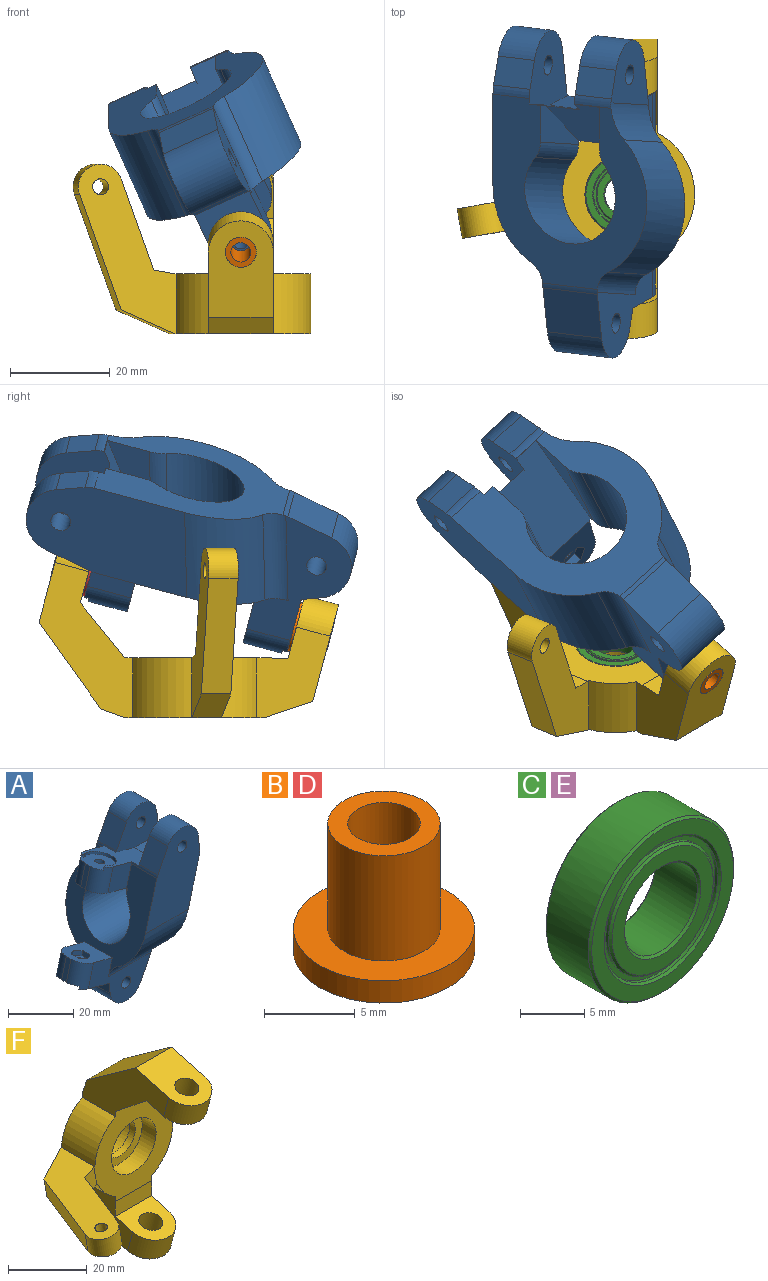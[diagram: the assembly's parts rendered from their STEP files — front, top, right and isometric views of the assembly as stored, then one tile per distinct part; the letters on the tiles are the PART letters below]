
ASSEMBLY  parts=6 mates=5
PART A: 77 faces, bbox 42.3x34x64 mm
  f0: cylinder r=1.6mm len=6.82mm, axis (0.26,0,0.97), area 62.3mm2, adj f56,f57
  f1: cylinder r=1.6mm len=6.82mm, axis (0.26,0,0.97), area 62.3mm2, adj f43,f44
  f2: plane 12.84x12mm, normal (-0.26,0,-0.97), area 122.6mm2, adj f3,f13,f14,f34,f45,f46,f47,f48
  f3: plane 7.73x2.07mm, normal (-0.97,0,0.26), area 16mm2, adj f2,f43,f69,f70
  f4: plane 19.08x15mm, normal (0.26,0,0.97), area 144.9mm2, adj f5,f6,f7,f13,f14,f38,f39,f40
  f5: plane 10.09x10mm, normal (0,0,1), area 81.8mm2, adj f4,f6,f7,f11,f33,f34
  f6: plane 18.49x15.03mm, normal (0,1,0), area 194.6mm2, adj f4,f5,f11,f18,f19,f20,f25,f73
  f7: plane 18.49x15.03mm, normal (0,-1,0), area 193.3mm2, adj f4,f5,f8,f11,f21,f22,f26,f34
  f8: plane 8.71x8mm, normal (-0.89,0,0.45), area 78.3mm2, adj f7,f22,f28,f64
  f9: plane 37.54x34mm, normal (-0.97,0,0.26), area 567.7mm2, adj f12,f13,f14,f15,f16,f17,f27,f29
  f10: plane 12x4.05mm, normal (-0.99,0,-0.11), area 48.9mm2, adj f17,f23,f27,f37
  f11: plane 36.58x34mm, normal (0.97,0,-0.26), area 622.7mm2, adj f5,f6,f7,f12,f15,f16,f29,f32
  f12: cylinder r=10mm len=23.05mm, axis (-1,0,0), area 845.3mm2, adj f9,f11,f65,f66
  f13: plane 10.84x10.48mm, normal (0,-1,0), area 75.6mm2, adj f2,f4,f9,f34,f70,f73
  f14: plane 10.84x10.48mm, normal (0,1,0), area 75.6mm2, adj f2,f4,f9,f34,f64,f69
  f15: cylinder r=17mm len=22.58mm, axis (-1,0,0), area 331.7mm2, adj f9,f11,f16,f76
  f16: plane 32x23.65mm, normal (0,-1,0), area 520mm2, adj f9,f11,f15,f18,f19,f20,f25,f73
  f17: plane 27.36x21.41mm, normal (0,-1,0), area 241.9mm2, adj f9,f10,f23,f24,f30,f36,f37,f68
  f18: plane 8x5.84mm, normal (0.99,0,0.11), area 47mm2, adj f6,f16,f19,f74
  f19: cylinder r=7mm len=13.19mm, axis (0,1,0), area 143.3mm2, adj f6,f16,f18,f20
  f20: plane 8.71x8mm, normal (-0.89,0,0.45), area 78.3mm2, adj f6,f16,f19,f73
  f21: plane 8x5.84mm, normal (0.99,0,0.11), area 47mm2, adj f7,f22,f28,f71
  f22: cylinder r=7mm len=13.19mm, axis (0,1,0), area 143.3mm2, adj f7,f8,f21,f28
  f23: cylinder r=7mm len=13.19mm, axis (0,1,0), area 214.9mm2, adj f10,f17,f24,f27
  f24: plane 12x8.71mm, normal (0.89,0,-0.45), area 117.4mm2, adj f17,f23,f27,f72
  f25: cylinder r=2mm len=8mm, axis (0,1,0), area 100.5mm2, adj f6,f16
  f26: cylinder r=2mm len=8mm, axis (0,1,0), area 100.5mm2, adj f7,f28
  f27: plane 27.36x21.41mm, normal (0,1,0), area 241.9mm2, adj f9,f10,f23,f24,f30,f36,f37,f67
  f28: plane 18.46x12.82mm, normal (0,1,0), area 162.6mm2, adj f8,f21,f22,f26,f35,f64,f71
  f29: cylinder r=17mm len=26.8mm, axis (-1,0,0), area 582.1mm2, adj f9,f11,f35,f75
  f30: cylinder r=2mm len=12mm, axis (0,1,0), area 150.8mm2, adj f17,f27
  f31: plane 7.73x2.07mm, normal (-0.97,0,0.26), area 16mm2, adj f36,f56,f67,f68
  f32: plane 20.88x8.37mm, normal (0,-1,0), area 85.9mm2, adj f9,f11,f34,f65
  f33: plane 20.6x7.34mm, normal (0,1,0), area 84.6mm2, adj f5,f9,f11,f34,f66
  f34: plane 20.77x13mm, normal (0.34,0,-0.94), area 264.6mm2, adj f2,f5,f7,f9,f11,f13,f14,f32
  f35: cylinder r=10mm len=20.41mm, axis (-1,0,0), area 147.2mm2, adj f9,f11,f28,f29,f64,f71
  f36: plane 12.94x12mm, normal (0.26,0,0.97), area 123.9mm2, adj f9,f17,f27,f31,f58,f59,f60,f61
  f37: plane 12.07x12mm, normal (-0.26,0,-0.97), area 74.3mm2, adj f10,f17,f27,f51,f52,f53,f54,f55
  f38: cylinder r=2mm len=1.12mm, axis (0.26,0,0.97), area 0.7mm2, adj f4,f39,f43,f69
  f39: cylinder r=0.6mm len=1.13mm, axis (0.26,0,0.97), area 0.7mm2, adj f4,f38,f40,f43
  f40: cylinder r=5.05mm len=10.1mm, axis (0.26,0,0.97), area 20.6mm2, adj f4,f39,f41,f43
  f41: cylinder r=0.6mm len=1.13mm, axis (0.26,0,0.97), area 0.7mm2, adj f4,f40,f42,f43
  f42: cylinder r=2mm len=1.12mm, axis (0.26,0,0.97), area 0.7mm2, adj f4,f41,f43,f70
  f43: plane 10.1x10.09mm, normal (0.26,0,0.97), area 79.7mm2, adj f1,f3,f38,f39,f40,f41,f42,f69
  f44: plane 6.35x5.31mm, normal (-0.26,0,-0.97), area 18.2mm2, adj f1,f45,f46,f47,f48,f49,f50
  f45: plane 3.18x1.74mm, normal (0.97,0,-0.26), area 5.7mm2, adj f2,f44,f46,f50
  f46: plane 3.12x2.45mm, normal (0.48,0.87,-0.13), area 5.7mm2, adj f2,f44,f45,f47
  f47: plane 3.12x2.45mm, normal (-0.48,0.87,0.13), area 5.7mm2, adj f2,f44,f46,f48
  f48: plane 3.18x1.74mm, normal (-0.97,0,0.26), area 5.7mm2, adj f2,f44,f47,f49
  f49: plane 3.12x2.45mm, normal (-0.48,-0.87,0.13), area 5.7mm2, adj f2,f44,f48,f50
  f50: plane 3.12x2.45mm, normal (0.48,-0.87,-0.13), area 5.7mm2, adj f2,f44,f45,f49
  f51: cylinder r=2mm len=1.12mm, axis (-0.26,0,-0.97), area 0.7mm2, adj f37,f52,f56,f68
  f52: cylinder r=0.6mm len=1.13mm, axis (-0.26,0,-0.97), area 0.7mm2, adj f37,f51,f53,f56
  f53: cylinder r=5.05mm len=10.1mm, axis (-0.26,0,-0.97), area 20.6mm2, adj f37,f52,f54,f56
  f54: cylinder r=0.6mm len=1.13mm, axis (-0.26,0,-0.97), area 0.7mm2, adj f37,f53,f55,f56
  f55: cylinder r=2mm len=1.12mm, axis (-0.26,0,-0.97), area 0.7mm2, adj f37,f54,f56,f67
  f56: plane 10.1x10.09mm, normal (-0.26,0,-0.97), area 79.7mm2, adj f0,f31,f51,f52,f53,f54,f55,f67
  f57: plane 6.35x5.31mm, normal (0.26,0,0.97), area 18.2mm2, adj f0,f58,f59,f60,f61,f62,f63
  f58: plane 3.18x1.74mm, normal (0.97,0,-0.26), area 5.7mm2, adj f36,f57,f59,f63
  f59: plane 3.12x2.45mm, normal (0.48,-0.87,-0.13), area 5.7mm2, adj f36,f57,f58,f60
  f60: plane 3.12x2.45mm, normal (-0.48,-0.87,0.13), area 5.7mm2, adj f36,f57,f59,f61
  f61: plane 3.18x1.74mm, normal (-0.97,0,0.26), area 5.7mm2, adj f36,f57,f60,f62
  f62: plane 3.12x2.45mm, normal (-0.48,0.87,0.13), area 5.7mm2, adj f36,f57,f61,f63
  f63: plane 3.12x2.45mm, normal (0.48,0.87,-0.13), area 5.7mm2, adj f36,f57,f58,f62
  f64: cylinder r=5mm len=8.02mm, axis (0,1,0), area 5.2mm2, adj f4,f7,f8,f9,f14,f28,f35
  f65: cylinder r=5mm len=19.5mm, axis (-1,0,0), area 65mm2, adj f9,f11,f12,f32
  f66: cylinder r=5mm len=19.5mm, axis (-1,0,0), area 65mm2, adj f9,f11,f12,f33
  f67: cylinder r=5mm len=9.99mm, axis (-0.26,0,-0.97), area 66.2mm2, adj f27,f31,f36,f37,f55,f56
  f68: cylinder r=5mm len=9.99mm, axis (-0.26,0,-0.97), area 66.2mm2, adj f17,f31,f36,f37,f51,f56
  f69: cylinder r=5mm len=9.99mm, axis (0.26,0,0.97), area 66.2mm2, adj f2,f3,f4,f14,f38,f43
  f70: cylinder r=5mm len=9.99mm, axis (-0.26,0,-0.97), area 66.2mm2, adj f2,f3,f4,f13,f42,f43
  f71: cylinder r=5mm len=8.06mm, axis (0,-1,0), area 14.9mm2, adj f7,f11,f21,f28,f35
  f72: cylinder r=5mm len=12.06mm, axis (0,1,0), area 12.6mm2, adj f11,f17,f24,f27,f75,f76
  f73: cylinder r=5mm len=11mm, axis (0,1,0), area 10.3mm2, adj f4,f6,f9,f13,f16,f20
  f74: cylinder r=5mm len=8mm, axis (0,-1,0), area 14.9mm2, adj f6,f11,f16,f18
  f75: cylinder r=5mm len=19.8mm, axis (-1,0,0), area 97.6mm2, adj f9,f11,f27,f29,f72
  f76: cylinder r=5mm len=19.8mm, axis (-1,0,0), area 97.6mm2, adj f9,f11,f15,f17,f72
PART B: 6 faces, bbox 10x10x8.6 mm
  f0: plane 10x10mm, normal (0,0,-1), area 66mm2, adj f1,f5
  f1: cylinder r=2mm len=8.6mm, axis (0,0,-1), area 108.1mm2, adj f0,f2
  f2: plane 6.2x6.2mm, normal (0,0,1), area 17.6mm2, adj f1,f3
  f3: cylinder r=3.1mm len=7.1mm, axis (0,0,-1), area 138.3mm2, adj f2,f4
  f4: plane 10x10mm, normal (0,0,1), area 48.3mm2, adj f3,f5
  f5: cylinder r=5mm len=10mm, axis (0,0,-1), area 47.1mm2, adj f0,f4
PART C: 20 faces, bbox 16x5x16 mm
  f0: cylinder r=8mm len=16mm, axis (0,-1,0), area 231.2mm2, adj f1,f2
  f1: cone r=8mm half-angle=45deg, axis (0,1,0), area 14mm2, adj f0,f14
  f2: cone r=8mm half-angle=45deg, axis (0,-1,0), area 14mm2, adj f0,f15
  f3: cone r=6.45mm half-angle=45deg, axis (0,-1,0), area 11.3mm2, adj f5,f14
  f4: cone r=6.45mm half-angle=45deg, axis (0,1,0), area 11.3mm2, adj f6,f15
  f5: cylinder r=6.25mm len=12.5mm, axis (0,-1,0), area 11.8mm2, adj f3,f16
  f6: cylinder r=6.25mm len=12.5mm, axis (0,-1,0), area 11.8mm2, adj f4,f17
  f7: cylinder r=5.75mm len=11.5mm, axis (0,-1,0), area 10.8mm2, adj f9,f16
  f8: cylinder r=5.75mm len=11.5mm, axis (0,-1,0), area 10.8mm2, adj f10,f17
  f9: cone r=5.75mm half-angle=45deg, axis (0,1,0), area 10mm2, adj f7,f18
  f10: cone r=5.75mm half-angle=45deg, axis (0,-1,0), area 10mm2, adj f8,f19
  f11: cone r=4.2mm half-angle=45deg, axis (0,-1,0), area 7.3mm2, adj f13,f18
  f12: cone r=4.2mm half-angle=45deg, axis (0,1,0), area 7.3mm2, adj f13,f19
  f13: cylinder r=4mm len=8mm, axis (0,-1,0), area 115.6mm2, adj f11,f12
  f14: plane 15.6x15.6mm, normal (0,-1,0), area 60.4mm2, adj f1,f3
  f15: plane 15.6x15.6mm, normal (0,1,0), area 60.4mm2, adj f2,f4
  f16: plane 12.5x12.5mm, normal (0,-1,0), area 18.8mm2, adj f5,f7
  f17: plane 12.5x12.5mm, normal (0,1,0), area 18.8mm2, adj f6,f8
  f18: plane 11.1x11.1mm, normal (0,-1,0), area 41.4mm2, adj f9,f11
  f19: plane 11.1x11.1mm, normal (0,1,0), area 41.4mm2, adj f10,f12
PART D: same geometry as B
PART E: same geometry as C
PART F: 35 faces, bbox 47.6x37.3x59.9 mm
  f0: cylinder r=14mm len=12mm, axis (0,1,0), area 175.8mm2, adj f3,f4,f9,f23
  f1: cylinder r=14mm len=12mm, axis (0,1,0), area 117.2mm2, adj f3,f4,f12,f22
  f2: cylinder r=14mm len=24.8mm, axis (0,1,0), area 365.6mm2, adj f3,f4,f11,f13
  f3: plane 28.31x28mm, normal (0,-1,0), area 428.9mm2, adj f0,f1,f2,f5,f9,f11,f12,f13
  f4: plane 28.31x28mm, normal (0,1,0), area 428.9mm2, adj f0,f1,f2,f9,f10,f11,f12,f13
  f5: plane 13x10.97mm, normal (0,-0.63,-0.78), area 183.1mm2, adj f3,f6,f9,f11
  f6: plane 13x12.56mm, normal (0,0.26,-0.97), area 120.7mm2, adj f5,f9,f11,f18,f21
  f7: plane 18.23x13mm, normal (0,-0.26,0.97), area 197mm2, adj f8,f9,f11,f18,f21
  f8: plane 17.4x13mm, normal (0,0.58,0.81), area 277.8mm2, adj f7,f9,f10,f11
  f9: plane 31.06x18.71mm, normal (-1,0,0), area 280.7mm2, adj f0,f3,f4,f5,f6,f7,f8,f10
  f10: plane 13x4.7mm, normal (0,0.94,0.34), area 65mm2, adj f4,f8,f9,f11
  f11: plane 31.06x18.71mm, normal (1,0,0), area 280.7mm2, adj f2,f3,f4,f5,f6,f7,f8,f10
  f12: plane 18.12x14.75mm, normal (-1,0,0), area 166.9mm2, adj f1,f3,f4,f14,f15,f16,f17,f19
  f13: plane 18.12x14.75mm, normal (1,0,0), area 166.9mm2, adj f2,f3,f4,f14,f15,f16,f17,f19
  f14: plane 13x4.7mm, normal (0,-1,-0.03), area 61.2mm2, adj f3,f12,f13,f15
  f15: plane 13x12.56mm, normal (0,-0.26,0.97), area 120.7mm2, adj f12,f13,f14,f19,f20
  f16: plane 19.32x13mm, normal (0,0.26,-0.97), area 211.7mm2, adj f12,f13,f17,f19,f20
  f17: plane 13x9.65mm, normal (0,0.95,-0.32), area 132.5mm2, adj f4,f12,f13,f16
  f18: cylinder r=6.5mm len=13mm, axis (0,-0.26,0.97), area 142.9mm2, adj f6,f7,f9,f11
  f19: cylinder r=6.5mm len=13mm, axis (0,-0.26,0.97), area 142.9mm2, adj f12,f13,f15,f16
  f20: cylinder r=3.1mm len=8.37mm, axis (0,0.26,-0.97), area 136.3mm2, adj f15,f16
  f21: cylinder r=3.1mm len=8.37mm, axis (0,0.26,-0.97), area 136.3mm2, adj f6,f7
  f22: plane 33.91x19.57mm, normal (0.17,0,-0.98), area 309.8mm2, adj f1,f3,f4,f24,f25,f26,f27,f28
  f23: plane 33.91x19.57mm, normal (-0.17,0,0.98), area 309.8mm2, adj f0,f3,f4,f24,f25,f26,f27,f28
  f24: cylinder r=4.5mm len=9.64mm, axis (-0.17,0,0.98), area 84.8mm2, adj f22,f23,f25,f29
  f25: plane 23.11x9.33mm, normal (-0.93,0.34,-0.16), area 147.6mm2, adj f22,f23,f24,f26
  f26: plane 11.73x7.79mm, normal (-0.4,0.92,-0.07), area 71.1mm2, adj f4,f22,f23,f25
  f27: plane 6.63x5.16mm, normal (0.17,-0.99,0.03), area 25.4mm2, adj f3,f22,f23,f29
  f28: cylinder r=1.6mm len=6.46mm, axis (-0.17,0,0.98), area 60.3mm2, adj f22,f23
  f29: plane 18.23x7.58mm, normal (0.93,-0.34,0.16), area 116.4mm2, adj f22,f23,f24,f27
  f30: cylinder r=8mm len=16mm, axis (0,1,0), area 251.3mm2, adj f4,f31
  f31: plane 16x16mm, normal (0,1,0), area 106mm2, adj f30,f32
  f32: cylinder r=5.5mm len=11mm, axis (0,1,0), area 69.1mm2, adj f31,f33
  f33: plane 16x16mm, normal (0,-1,0), area 106mm2, adj f32,f34
  f34: cylinder r=8mm len=16mm, axis (0,1,0), area 251.3mm2, adj f3,f33
PLACE A rot(axis=(-0.44,-0.6,-0.66),138.3deg) t=(-36.6,1.59,105.31)mm
PLACE B rot(axis=(0.66,0.6,-0.46),126.6deg) t=(0.02,-18.93,18.51)mm
PLACE C rot(axis=(-1,0,0),90deg) t=(0.02,0,9.5)mm
PLACE D rot(axis=(-0.69,0.44,0.57),96deg) t=(0.02,19.7,28.86)mm
PLACE E rot(axis=(-1,0,0),90deg) t=(0.02,0,2.5)mm
PLACE F rot(axis=(-1,0,0),90deg) t=(0.02,0,0)mm
MATE revolute D.f1 <-> F.f18  axis (0,0.97,0.26) through (0.02,21.15,29.25)mm
MATE fastened D.f1 <-> A.f0  axis (0,-0.97,-0.26) through (0.02,19.7,28.86)mm
MATE revolute E.f0 <-> C.f0  axis (0,0,-1) through (0.02,0,0)mm
MATE revolute B.f1 <-> F.f18  axis (0,-0.97,-0.26) through (0.02,-20.38,18.12)mm
MATE revolute E.f0 <-> F.f30  axis (0,0,-1) through (0.02,0,0)mm
